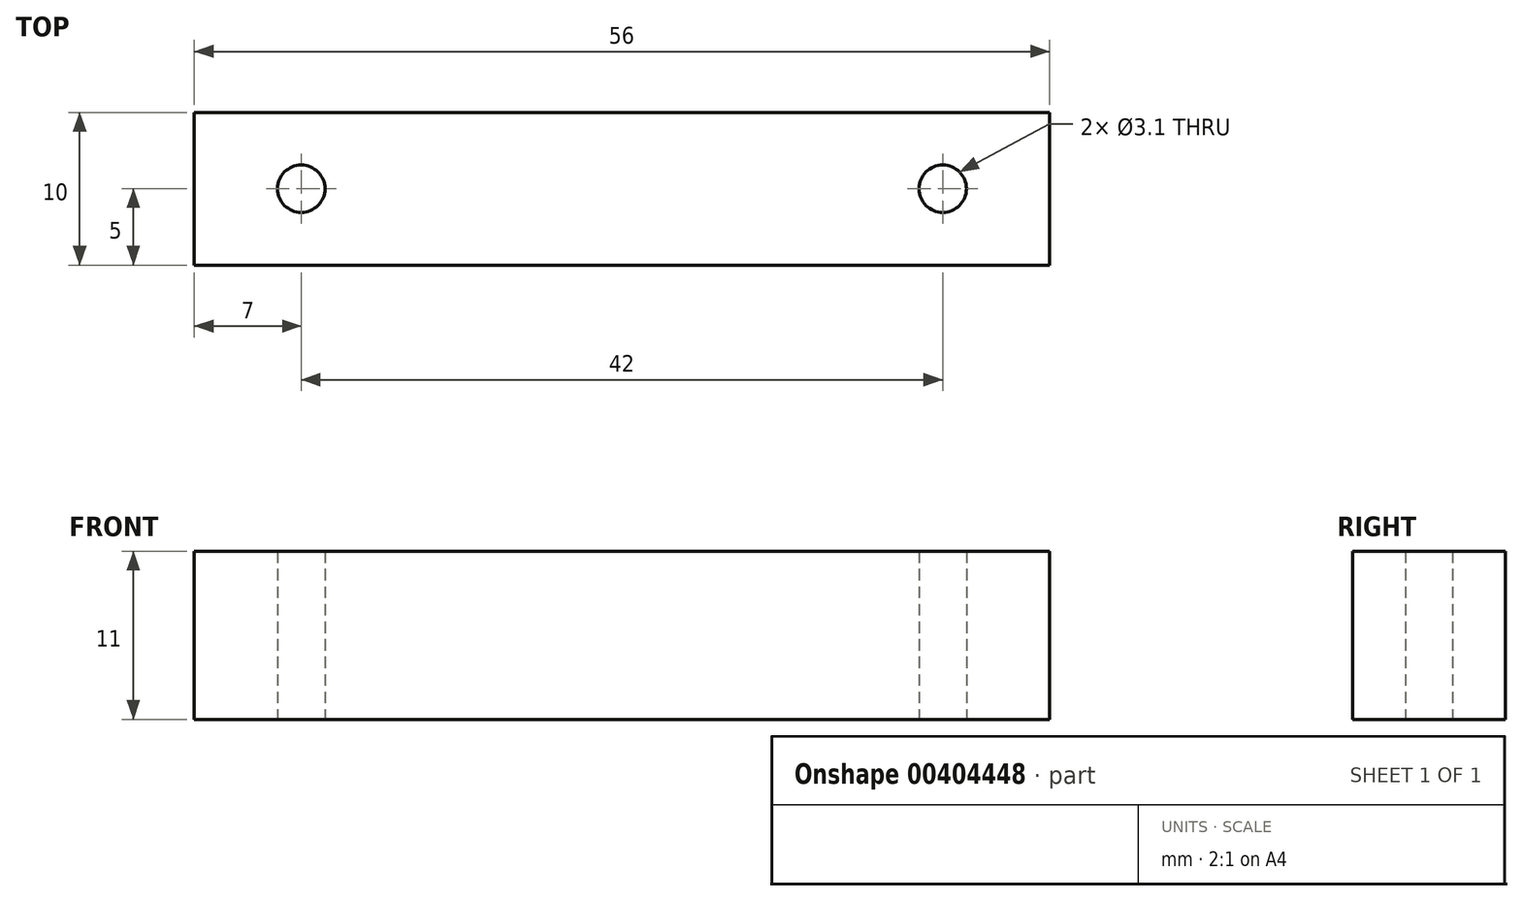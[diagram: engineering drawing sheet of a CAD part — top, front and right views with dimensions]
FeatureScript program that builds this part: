
annotation { "Feature Type Name" : "Feature", "Feature Type Description" : "" }
export const myFeature = defineFeature(function(context is Context, id is Id, definition is map)
    precondition{}
    {
        {
            var Q0;
            Q0=qCreatedBy(makeId("Top.planeOp"),FACE);
            var sketch = newSketch(context, id + "F0", { "sketchPlane" : qUnion([Q0])});
            skLineSegment(sketch, "E0.bottom", {"start": v(-28, 5) * mm, "end": v(28, 5) * mm});
            skLineSegment(sketch, "E0.top", {"start": v(-28, -5) * mm, "end": v(28, -5) * mm});
            skLineSegment(sketch, "E0.left", {"start": v(-28, 5) * mm, "end": v(-28, -5) * mm});
            skLineSegment(sketch, "E0.right", {"start": v(28, 5) * mm, "end": v(28, -5) * mm});
            skPoint(sketch, "E0.middle", {"position": v(0, 0) * mm});
            skLineSegment(sketch, "E1", {"start": v(-21, 0) * mm, "end": v(21, 0) * mm});
            skSolve(sketch);
        }
        {
            var Q0;
            Q0 = qSketchRegion(id + "F0", true);
            extrude(context, id + "F1", {"entities" : qUnion([Q0]), "depth" : 11 * mm});
        }
        {
            var Q0;
            Q0=sQuery(id+"F0.wireOp",VERTEX,"E1.end");
            var Q1;
            Q1=sQuery(id+"F0.wireOp",VERTEX,"E1.start");
            var Q2;
            Q2=makeQuery(id+"F1.opExtrude","SWEPT_BODY",BODY,{"disambiguationData":[OSD([sQuery(id+"F0.wireOp",EDGE,"E0.bottom"),sQuery(id+"F0.wireOp",EDGE,"E0.top"),sQuery(id+"F0.wireOp",EDGE,"E0.left"),sQuery(id+"F0.wireOp",EDGE,"E0.right")])]});
            hole(context, id + "F2", {"style" : HoleStyle.SIMPLE, "endStyle" : HoleEndStyle.THROUGH, "oppositeDirection" : true, "holeDiameter" : 3.1 * mm, "tappedDepth" : 12 * mm, "tapClearance" : 3, "locations" : qUnion([Q0, Q1]), "scope" : qUnion([Q2])});
        }
    });
